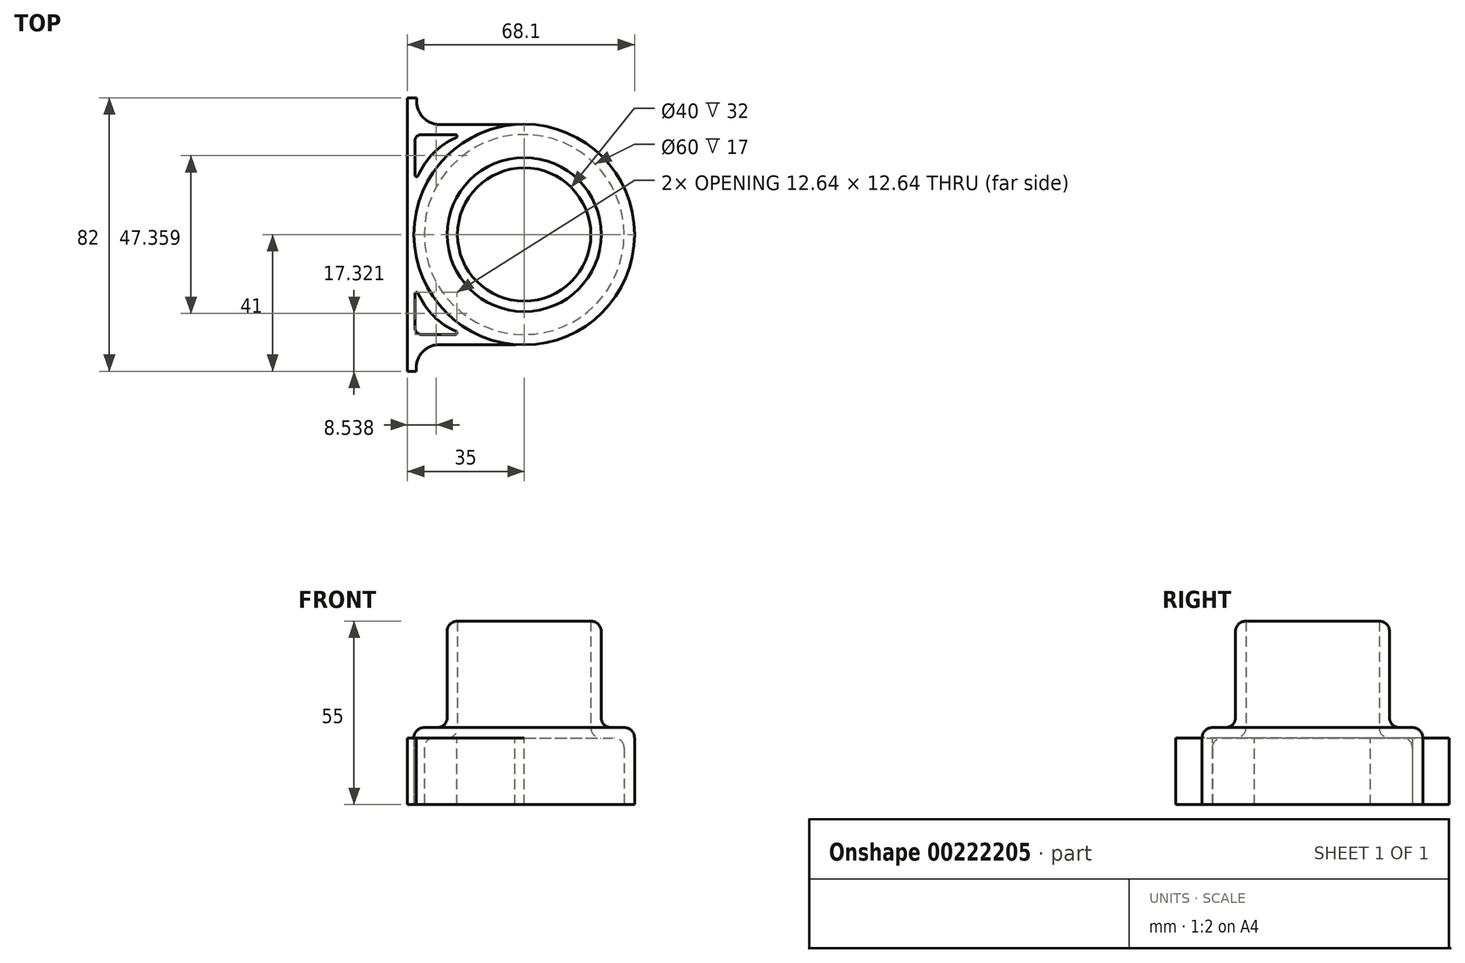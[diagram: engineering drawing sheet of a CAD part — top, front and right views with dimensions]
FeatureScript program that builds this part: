
annotation { "Feature Type Name" : "Feature", "Feature Type Description" : "" }
export const myFeature = defineFeature(function(context is Context, id is Id, definition is map)
    precondition{}
    {
        {
            var Q0;
            Q0=qCreatedBy(makeId("Top.planeOp"),FACE);
            var sketch = newSketch(context, id + "F0", { "sketchPlane" : qUnion([Q0])});
            skArc(sketch, "E0", {"start": v(-33, 0) * mm, "mid": v(-23.33, -23.33) * mm, "end": v(0, -33) * mm});
            skLineSegment(sketch, "E1", {"start": v(0, -33) * mm, "end": v(-25.39, -33) * mm});
            skLineSegment(sketch, "E2", {"start": v(-32.39, -40.1) * mm, "end": v(-32.37, -41) * mm});
            skLineSegment(sketch, "E3", {"start": v(-35, -3) * mm, "end": v(-35, -41) * mm});
            skPoint(sketch, "E4.orphan", {"position": v(-40.2, 0) * mm});
            skArc(sketch, "E5.filletArc", {"start": v(-25.39, -33) * mm, "mid": v(-30.68, -35.42) * mm, "end": v(-32.32, -41) * mm});
            skLineSegment(sketch, "E6", {"start": v(-35, -41) * mm, "end": v(-32.32, -41) * mm});
            skPoint(sketch, "E7", {"position": v(-33.5, -38) * mm});
            skLineSegment(sketch, "E8.MirrorCS", {"start": v(-35, 41) * mm, "end": v(-32.18, 41) * mm});
            skLineSegment(sketch, "E9.MirrorCS", {"start": v(-29.43, 37.1) * mm, "end": v(-29.42, 38) * mm});
            skPoint(sketch, "E10.MirrorP", {"position": v(-30.68, 35) * mm});
            skArc(sketch, "E11.MirrorCS", {"start": v(-33, 0) * mm, "mid": v(-24.35, 22.4) * mm, "end": v(-2.82, 33) * mm});
            skArc(sketch, "E12.MirrorCS", {"start": v(-25.25, 33) * mm, "mid": v(-30.54, 35.42) * mm, "end": v(-32.18, 41) * mm});
            skLineSegment(sketch, "E13.MirrorCS", {"start": v(-35, 0) * mm, "end": v(-35, 41) * mm});
            skLineSegment(sketch, "E14.MirrorCS", {"start": v(-2.82, 33) * mm, "end": v(-25.25, 33) * mm});
            skLineSegment(sketch, "E15", {"start": v(-35, -3) * mm, "end": v(-35, 0) * mm});
            skLineSegment(sketch, "E16", {"start": v(-32.78, -15) * mm, "end": v(-32.78, -30) * mm});
            skLineSegment(sketch, "E17", {"start": v(-32.78, -30) * mm, "end": v(-17.78, -30) * mm});
            skArc(sketch, "E18", {"start": v(-32.78, -15) * mm, "mid": v(-27.2, -24.43) * mm, "end": v(-17.78, -30) * mm});
            skArc(sketch, "E19.MirrorCS", {"start": v(-32.78, 15) * mm, "mid": v(-27.2, 24.43) * mm, "end": v(-17.78, 30) * mm});
            skLineSegment(sketch, "E20.MirrorCS", {"start": v(-32.78, 15) * mm, "end": v(-32.78, 30) * mm});
            skLineSegment(sketch, "E21.MirrorCS", {"start": v(-32.78, 30) * mm, "end": v(-17.78, 30) * mm});
            skPoint(sketch, "E22.MirrorP", {"position": v(-33.5, 38) * mm});
            skSolve(sketch);
        }
        {
            var Q0;
            Q0=qCreatedBy(makeId("Front.planeOp"),FACE);
            var sketch = newSketch(context, id + "F1", { "sketchPlane" : qUnion([Q0])});
            skLineSegment(sketch, "E23", {"start": v(0, 0) * mm, "end": v(0, 20.23) * mm});
            skLineSegment(sketch, "E24", {"start": v(-20, 35) * mm, "end": v(-20, 3) * mm});
            skLineSegment(sketch, "E25", {"start": v(-23, 0) * mm, "end": v(-27, 0) * mm});
            skLineSegment(sketch, "E26", {"start": v(-30, -3) * mm, "end": v(-30, -20) * mm});
            skLineSegment(sketch, "E27", {"start": v(-30, -20) * mm, "end": v(-33.1, -20) * mm});
            skLineSegment(sketch, "E28.0", {"start": v(-33.1, 0.1) * mm, "end": v(-33.1, -19.9) * mm});
            skLineSegment(sketch, "E28.1", {"start": v(-26.1, 3.1) * mm, "end": v(-30.1, 3.1) * mm});
            skLineSegment(sketch, "E28.2", {"start": v(-23.1, 32) * mm, "end": v(-23.1, 6.1) * mm});
            skLineSegment(sketch, "E29", {"start": v(-20, 35) * mm, "end": v(-20.1, 35) * mm});
            skPoint(sketch, "E30.visualSharp", {"position": v(-30, 0) * mm});
            skArc(sketch, "E30.filletArc", {"start": v(-27, 0) * mm, "mid": v(-29.12, -0.88) * mm, "end": v(-30, -3) * mm});
            skPoint(sketch, "E31.visualSharp", {"position": v(-33.1, 3.1) * mm});
            skArc(sketch, "E31.filletArc", {"start": v(-30.1, 3.1) * mm, "mid": v(-32.22, 2.22) * mm, "end": v(-33.1, 0.1) * mm});
            skPoint(sketch, "E32.visualSharp", {"position": v(-23.1, 3.1) * mm});
            skArc(sketch, "E32.filletArc", {"start": v(-26.1, 3.1) * mm, "mid": v(-23.98, 3.98) * mm, "end": v(-23.1, 6.1) * mm});
            skPoint(sketch, "E33.visualSharp", {"position": v(-20, 0) * mm});
            skArc(sketch, "E33.filletArc", {"start": v(-23, 0) * mm, "mid": v(-20.88, 0.88) * mm, "end": v(-20, 3) * mm});
            skPoint(sketch, "E34.visualSharp", {"position": v(-23.1, 35) * mm});
            skArc(sketch, "E34.filletArc", {"start": v(-20.1, 35) * mm, "mid": v(-22.22, 34.12) * mm, "end": v(-23.1, 32) * mm});
            skLineSegment(sketch, "E35", {"start": v(-33.1, -20) * mm, "end": v(-33.1, -19.9) * mm});
            skSolve(sketch);
        }
        {
            var Q0;
            Q0=makeQuery(id+"F1.imprint","IMPRINT",FACE,{"disambiguationData":[TD([[makeQuery(id+"F1.imprint","IMPRINT",EDGE,{"derivedFrom":sQuery(id+"F1.wireOp",EDGE,"E24")}),-1.0]])]});
            var Q1;
            Q1=sQuery(id+"F1.wireOp",EDGE,"E23");
            revolve(context, id + "F2", {"entities" : qUnion([Q0]), "axis" : qUnion([Q1]), "revolveType" : RevolveType.FULL});
        }
        {
            var Q0;
            Q0=makeQuery(id+"F0.imprint","IMPRINT",FACE,{"disambiguationData":[TD([[makeQuery(id+"F0.imprint","IMPRINT",EDGE,{"derivedFrom":sQuery(id+"F0.wireOp",EDGE,"E0")}),-1.0]])]});
            extrude(context, id + "F3", {"entities" : qUnion([Q0]), "oppositeDirection" : true, "depth" : 20 * mm});
        }
        {
            var Q0;
            Q0=qCreatedBy(makeId("Right.planeOp"),FACE);
            cPlane(context, id + "F4", {"entities" : qUnion([Q0]), "cplaneType" : CPlaneType.OFFSET, "offset" : 35 * mm, "oppositeDirection" : true, "width" : 150 * mm, "height" : 150 * mm});
        }
        {
            var Q0;
            Q0=qCreatedBy(id+"F4.planeOp",FACE);
            var sketch = newSketch(context, id + "F5", { "sketchPlane" : qUnion([Q0])});
            skPoint(sketch, "E36", {"position": v(36, -3) * mm});
            skPoint(sketch, "E37", {"position": v(36, -17) * mm});
            skPoint(sketch, "E38", {"position": v(-36.13, -17) * mm});
            skPoint(sketch, "E39", {"position": v(-36, -3) * mm});
            skSolve(sketch);
        }
        {
            var Q0;
            Q0=sQuery(id+"F5.wireOp",VERTEX,"E39");
            var Q1;
            Q1=sQuery(id+"F5.wireOp",VERTEX,"E38");
            var Q2;
            Q2=sQuery(id+"F5.wireOp",VERTEX,"E37");
            var Q3;
            Q3=sQuery(id+"F5.wireOp",VERTEX,"E36");
            var Q4;
            Q4=makeQuery(id+"F2.opRevolve","SWEPT_BODY",BODY,{"disambiguationData":[OSD([sQuery(id+"F1.wireOp",EDGE,"E24"),sQuery(id+"F1.wireOp",EDGE,"E25"),sQuery(id+"F1.wireOp",EDGE,"E26"),sQuery(id+"F1.wireOp",EDGE,"E27"),sQuery(id+"F1.wireOp",EDGE,"E28.0"),sQuery(id+"F1.wireOp",EDGE,"E28.1"),sQuery(id+"F1.wireOp",EDGE,"E28.2"),sQuery(id+"F1.wireOp",EDGE,"E29"),sQuery(id+"F1.wireOp",EDGE,"E30.filletArc"),sQuery(id+"F1.wireOp",EDGE,"E31.filletArc"),sQuery(id+"F1.wireOp",EDGE,"E32.filletArc"),sQuery(id+"F1.wireOp",EDGE,"E33.filletArc"),sQuery(id+"F1.wireOp",EDGE,"E34.filletArc"),sQuery(id+"F1.wireOp",EDGE,"E35")])]});
            hole(context, id + "F6", {"style" : HoleStyle.SIMPLE, "endStyle" : HoleEndStyle.THROUGH, "oppositeDirection" : true, "holeDiameter" : 3 * mm, "startFromSketch" : true, "locations" : qUnion([Q0, Q1, Q2, Q3]), "scope" : qUnion([Q4]), "isTappedThrough" : true});
        }
        {
            var Q0;
            Q0=makeQuery(id+"F3.opExtrude","SWEPT_EDGE",EDGE,{"disambiguationData":[OSD([sQuery(id+"F0.wireOp",EDGE,"E20.MirrorCS"),sQuery(id+"F0.wireOp",EDGE,"E21.MirrorCS")])]});
            fillet(context, id + "F7", {"entities" : qUnion([Q0]), "radius" : 2 * mm, "tangentPropagation" : true, "allowEdgeOverflow" : false});
        }
        {
            var Q0;
            Q0=makeQuery(id+"F3.opExtrude","SWEPT_EDGE",EDGE,{"disambiguationData":[OSD([sQuery(id+"F0.wireOp",EDGE,"E16"),sQuery(id+"F0.wireOp",EDGE,"E17")])]});
            fillet(context, id + "F8", {"entities" : qUnion([Q0]), "radius" : 2 * mm, "tangentPropagation" : true, "allowEdgeOverflow" : false});
        }
        {
            var Q0;
            Q0=makeQuery(id+"F3.opExtrude","SWEPT_EDGE",EDGE,{"disambiguationData":[OSD([sQuery(id+"F0.wireOp",EDGE,"E16"),sQuery(id+"F0.wireOp",EDGE,"E18")])]});
            var Q1;
            Q1=makeQuery(id+"F3.opExtrude","SWEPT_EDGE",EDGE,{"disambiguationData":[OSD([sQuery(id+"F0.wireOp",EDGE,"E17"),sQuery(id+"F0.wireOp",EDGE,"E18")])]});
            var Q2;
            Q2=makeQuery(id+"F3.opExtrude","SWEPT_EDGE",EDGE,{"disambiguationData":[OSD([sQuery(id+"F0.wireOp",EDGE,"E19.MirrorCS"),sQuery(id+"F0.wireOp",EDGE,"E21.MirrorCS")])]});
            var Q3;
            Q3=makeQuery(id+"F3.opExtrude","SWEPT_EDGE",EDGE,{"disambiguationData":[OSD([sQuery(id+"F0.wireOp",EDGE,"E19.MirrorCS"),sQuery(id+"F0.wireOp",EDGE,"E20.MirrorCS")])]});
            fillet(context, id + "F9", {"entities" : qUnion([Q0, Q1, Q2, Q3]), "radius" : 0.5 * mm, "tangentPropagation" : true, "allowEdgeOverflow" : false});
        }
    });
